# Revit family: DALI Repeater_406
name_source: partatom
category: Electrical Fixtures
revit_build: Autodesk Revit 2018 (Build: 20170223_1515(x64)
units: mm (PartAtom-declared; Revit-internal decimal feet)

## family parameters
Always vertical = Yes
Cut with Voids When Loaded = No
Maintain Annotation Orientation = No
OmniClass Number = 23.80.00.00
OmniClass Title = Electric Power and Lighting
Part Type = Normal
Room Calculation Point = No
Round Connector Dimension = Use Diameter
Shared = No
Work Plane-Based = Yes

## types (1)
- DALI Repeater (DIN Rail) with integral 250mA POWER SUPPLY
    Ambient temperature = –20 °C to +50 °C
    DALI cable = 0.5 mm² – 1.5 mm²
DALI cables must be mains rated.
    DALI consumption = 2 mA (DALI-IN side)
    DALI standard = IEC 62386-101
    DALI-OUT current: = 250 mA
    Default Elevation = 0 mm  [stored 0 ft]
    Dimensions: = 35 mm × 90 mm × 58 mm
    EMC emission = EN 55015
    EMC immunity = EN 61547
    Electrical data = Supply:                        100 VAC – 240 VAC (nominal)
                                    85 VAC – 264 VAC (absolute)
                                    48 Hz – 62 Hz
Current consumption: 100 mA
External protection:    6 A MCB maximum
Mains cable:                0.5 mm² – 1.5 mm² solid or stranded
    Environment = Complies with WEEE and RoHS
directives.
    IP code: = IP20
    Manufacturer = Helvar
    Model = 406
    Mounting = DIN rail (installation in switchgear/controlgear cabinet)
    Relative humidity = Max. 90 %, noncondensing
    Safety = EN 61347-2-11
    Storage temperature = −10 °C to + 70 °C
    Weight: = 90 g

note: [stored X ft] marks values corroborated as IEEE doubles in the binary element streams (Revit-internal decimal feet)

## geometry (parser evidence)
native form markers: Sweep x1
no freeform markers — native parametric forms only
